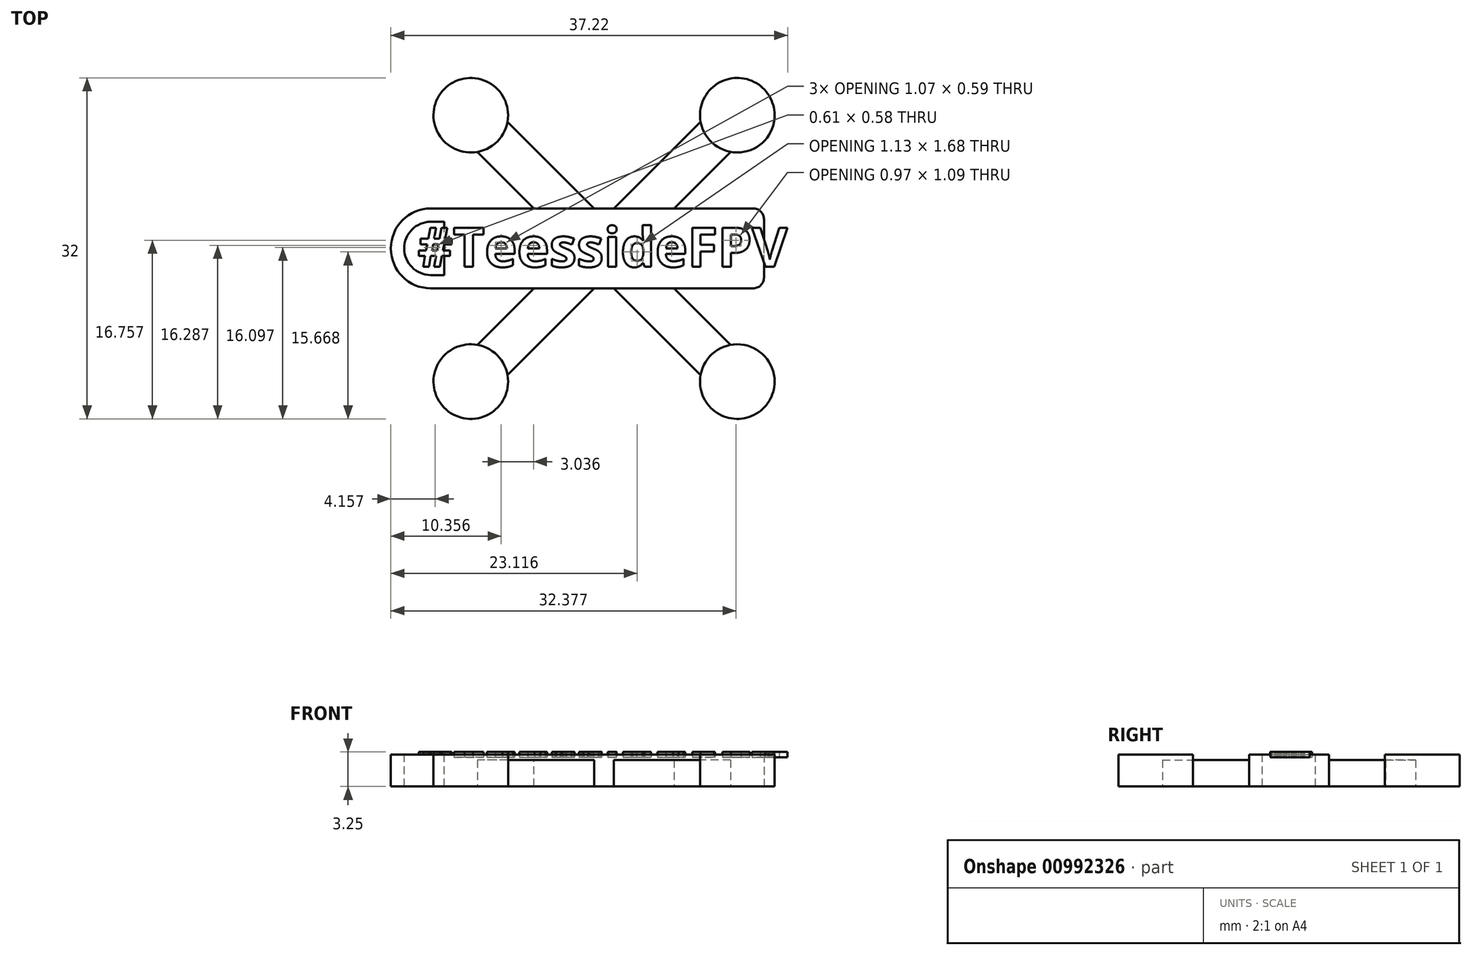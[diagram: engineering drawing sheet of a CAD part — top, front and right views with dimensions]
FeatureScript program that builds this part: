
annotation { "Feature Type Name" : "Feature", "Feature Type Description" : "" }
export const myFeature = defineFeature(function(context is Context, id is Id, definition is map)
    precondition{}
    {
        {
            assignVariable(context, id + "F0", {"name" : "Length", "anyValue" : 30});
        }
        {
            var Q0;
            Q0=qCreatedBy(makeId("Top.planeOp"),FACE);
            var sketch = newSketch(context, id + "F1", { "sketchPlane" : qUnion([Q0])});
            skLineSegment(sketch, "E0.bottom", {"start": v(15, -3.75) * mm, "end": v(-15, -3.75) * mm});
            skLineSegment(sketch, "E0.top", {"start": v(15, 3.75) * mm, "end": v(-15, 3.75) * mm});
            skLineSegment(sketch, "E0.left", {"start": v(15, -3.75) * mm, "end": v(15, 3.75) * mm});
            skLineSegment(sketch, "E0.right", {"start": v(-15, -3.75) * mm, "end": v(-15, 3.75) * mm});
            skPoint(sketch, "E0.middle", {"position": v(0, 0) * mm});
            skCircle(sketch, "E1", {"center": v(-12.5, 12.5) * mm, "radius": 3.5 * mm});
            skCircle(sketch, "E2", {"center": v(-12.5, -12.5) * mm, "radius": 3.5 * mm});
            skCircle(sketch, "E3", {"center": v(12.5, -12.5) * mm, "radius": 3.5 * mm});
            skCircle(sketch, "E4", {"center": v(12.5, 12.5) * mm, "radius": 3.5 * mm});
            skSolve(sketch);
        }
        {
            var Q0;
            Q0=qSketchRegion(id+"F1",true);
            extrude(context, id + "F2", {"entities" : qUnion([Q0]), "depth" : 3 * mm, "offsetDistance" : 25 * mm});
        }
        {
            var Q0;
            Q0=makeQuery(id+"F2.opExtrude","CAP_FACE",FACE,{"disambiguationData":[OSD([sQuery(id+"F1.wireOp",EDGE,"E0.bottom"),sQuery(id+"F1.wireOp",EDGE,"E0.top"),sQuery(id+"F1.wireOp",EDGE,"E0.left"),sQuery(id+"F1.wireOp",EDGE,"E0.right")])],"isStart":false});
            var sketch = newSketch(context, id + "F3", { "sketchPlane" : qUnion([Q0])});
            skText(sketch, "E5", { "text": "#TeessideFPV", "fontName": "OpenSans-Bold.ttf"});
            const initialGuessF3  = {"E5": [-0.0175, -0.00173, 1, 0, 0.0037]};
            skSetInitialGuess(sketch, initialGuessF3);
            skSolve(sketch);
        }
        {
            var Q0;
            Q0=qSketchRegion(id+"F3",true);
            extrude(context, id + "F4", {"entities" : qUnion([Q0]), "endBound" : BoundingType.SYMMETRIC, "depth" : 0.5 * mm, "offsetDistance" : 25 * mm});
        }
        {
            var Q0;
            Q0=makeQuery(id+"F2.opExtrude","CAP_FACE",FACE,{"disambiguationData":[OSD([sQuery(id+"F1.wireOp",EDGE,"E0.bottom"),sQuery(id+"F1.wireOp",EDGE,"E0.top"),sQuery(id+"F1.wireOp",EDGE,"E0.left"),sQuery(id+"F1.wireOp",EDGE,"E0.right")])],"isStart":true});
            var sketch = newSketch(context, id + "F5", { "sketchPlane" : qUnion([Q0])});
            skLineSegment(sketch, "E6.bottom", {"start": v(11.09, 13.91) * mm, "end": v(-13.91, -11.09) * mm});
            skLineSegment(sketch, "E6.top", {"start": v(13.91, 11.09) * mm, "end": v(-11.09, -13.91) * mm});
            skLineSegment(sketch, "E6.left", {"start": v(11.09, 13.91) * mm, "end": v(13.91, 11.09) * mm});
            skLineSegment(sketch, "E6.right", {"start": v(-13.91, -11.09) * mm, "end": v(-11.09, -13.91) * mm});
            skPoint(sketch, "E6.middle", {"position": v(0, 0) * mm});
            skLineSegment(sketch, "E7.bottom", {"start": v(13.91, -11.09) * mm, "end": v(-11.09, 13.91) * mm});
            skLineSegment(sketch, "E7.top", {"start": v(11.09, -13.91) * mm, "end": v(-13.91, 11.09) * mm});
            skLineSegment(sketch, "E7.left", {"start": v(13.91, -11.09) * mm, "end": v(11.09, -13.91) * mm});
            skLineSegment(sketch, "E7.right", {"start": v(-11.09, 13.91) * mm, "end": v(-13.91, 11.09) * mm});
            skSolve(sketch);
        }
        {
            var Q0;
            Q0=qSketchRegion(id+"F5",true);
            extrude(context, id + "F6", {"entities" : qUnion([Q0]), "operationType" : NewBodyOperationType.ADD, "oppositeDirection" : true, "depth" : 2.5 * mm, "offsetDistance" : 25 * mm});
        }
        {
            var Q0;
            Q0=makeQuery(id+"F2.opExtrude","SWEPT_FACE",FACE,{"disambiguationData":[OSD([sQuery(id+"F1.wireOp",EDGE,"E0.right")])]});
            extrude(context, id + "F7", {"entities" : qUnion([Q0]), "operationType" : NewBodyOperationType.ADD, "depth" : 5 * mm, "offsetDistance" : 25 * mm});
        }
        {
            var Q0;
            Q0=makeQuery(id+"F7.opExtrude","CAP_EDGE",EDGE,{"disambiguationData":[OSD([sQuery(id+"F1.wireOp",EDGE,"E0.top"),sQuery(id+"F1.wireOp",EDGE,"E0.right")])],"isStart":false});
            var Q1;
            Q1=makeQuery(id+"F7.opExtrude","CAP_EDGE",EDGE,{"disambiguationData":[OSD([sQuery(id+"F1.wireOp",EDGE,"E0.bottom"),sQuery(id+"F1.wireOp",EDGE,"E0.right")])],"isStart":false});
            fillet(context, id + "F8", {"entities" : qUnion([Q0, Q1]), "radius" : (getVariable(context, 'Length') / 8) * mm, "tangentPropagation" : true, "allowEdgeOverflow" : false});
        }
        {
            var Q0;
            {var subQ0=sQuery(id+"F1.wireOp",EDGE,"E0.right");var subQ1=sQuery(id+"F1.wireOp",EDGE,"E0.top");var subQ2=sQuery(id+"F1.wireOp",EDGE,"E0.bottom");var subQ3=sQuery(id+"F1.wireOp",EDGE,"E0.left");Q0=makeQuery(id+"F7.boolean.opBoolean","MERGE",FACE,{"derivedFrom":[makeQuery(id+"F4.boolean.opBoolean","SPLIT",FACE,{"disambiguationData":[TD([makeQuery(id+"F2.opExtrude","SWEPT_FACE",FACE,{"disambiguationData":[OSD([subQ2])]})])],"derivedFrom":makeQuery(id+"F2.opExtrude","CAP_FACE",FACE,{"disambiguationData":[OSD([subQ2,subQ1,subQ3,subQ0])],"isStart":false})}),makeQuery(id+"F7.opExtrude","SWEPT_FACE",FACE,{"disambiguationData":[OSD([subQ0]),TDD([makeQuery(id+"F2.opExtrude","CAP_EDGE",EDGE,{"disambiguationData":[OSD([subQ0])],"isStart":false})])]})]});}
            var sketch = newSketch(context, id + "F9", { "sketchPlane" : qUnion([Q0])});
            skArc(sketch, "E8", {"start": v(-16.25, 2.5) * mm, "mid": v(-18.75, 0) * mm, "end": v(-16.25, -2.5) * mm});
            skLineSegment(sketch, "E9", {"start": v(-16.25, 2.5) * mm, "end": v(-15, 2.5) * mm});
            skLineSegment(sketch, "E10", {"start": v(-16.25, -2.5) * mm, "end": v(-15, -2.5) * mm});
            skLineSegment(sketch, "E11.3", {"start": v(-15, -2.5) * mm, "end": v(-15, 2.5) * mm});
            skPoint(sketch, "E11.4", {"position": v(0, 0) * mm});
            skPoint(sketch, "E11.1.end.orphan", {"position": v(-15, 3.75) * mm});
            skPoint(sketch, "E11.1.start.orphan", {"position": v(15, 3.75) * mm});
            skPoint(sketch, "E11.2.end.orphan", {"position": v(15, 3.75) * mm});
            skPoint(sketch, "E11.2.start.orphan", {"position": v(15, -3.75) * mm});
            skPoint(sketch, "E11.0.end.orphan", {"position": v(-15, -3.75) * mm});
            skPoint(sketch, "E11.0.start.orphan", {"position": v(15, -3.75) * mm});
            skSolve(sketch);
        }
        {
            var Q0;
            Q0=qSketchRegion(id+"F9",true);
            extrude(context, id + "F10", {"entities" : qUnion([Q0]), "operationType" : NewBodyOperationType.REMOVE, "oppositeDirection" : true, "depth" : 25 * mm, "offsetDistance" : 25 * mm});
        }
        {
            var Q0;
            Q0=makeQuery(id+"F2.opExtrude","SWEPT_EDGE",EDGE,{"disambiguationData":[OSD([sQuery(id+"F1.wireOp",EDGE,"E0.bottom"),sQuery(id+"F1.wireOp",EDGE,"E0.left")])]});
            var Q1;
            Q1=makeQuery(id+"F2.opExtrude","SWEPT_EDGE",EDGE,{"disambiguationData":[OSD([sQuery(id+"F1.wireOp",EDGE,"E0.top"),sQuery(id+"F1.wireOp",EDGE,"E0.left")])]});
            fillet(context, id + "F11", {"entities" : qUnion([Q0, Q1]), "radius" : 1 * mm, "tangentPropagation" : true, "allowEdgeOverflow" : false});
        }
    });
